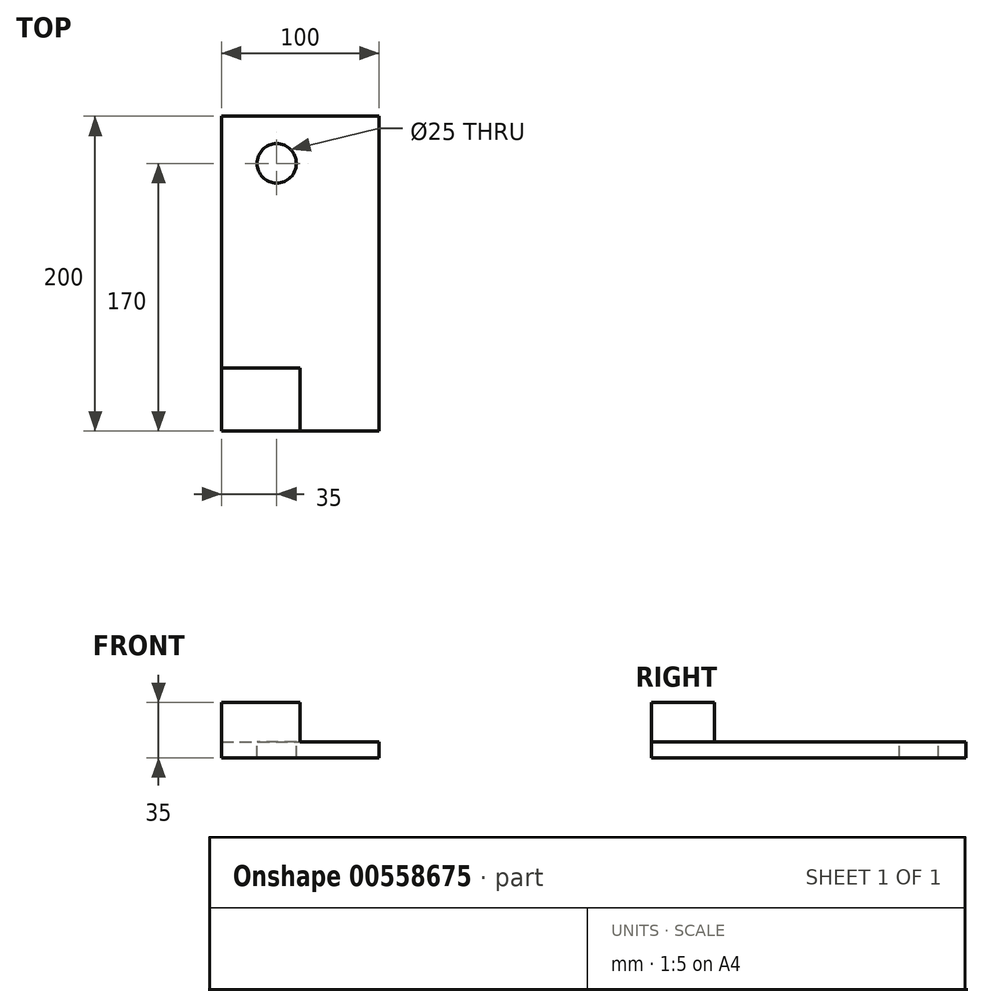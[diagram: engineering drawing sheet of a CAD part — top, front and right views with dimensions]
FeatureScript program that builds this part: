
annotation { "Feature Type Name" : "Feature", "Feature Type Description" : "" }
export const myFeature = defineFeature(function(context is Context, id is Id, definition is map)
    precondition{}
    {
        {
            var Q0;
            Q0=qCreatedBy(makeId("Top.planeOp"),FACE);
            var sketch = newSketch(context, id + "F0", { "sketchPlane" : qUnion([Q0])});
            skLineSegment(sketch, "E0.bottom", {"start": v(0, 0) * mm, "end": v(100, 0) * mm});
            skLineSegment(sketch, "E0.top", {"start": v(0, 200) * mm, "end": v(100, 200) * mm});
            skLineSegment(sketch, "E0.left", {"start": v(0, 0) * mm, "end": v(0, 200) * mm});
            skLineSegment(sketch, "E0.right", {"start": v(100, 0) * mm, "end": v(100, 200) * mm});
            skSolve(sketch);
        }
        {
            var Q0;
            Q0 = qSketchRegion(id + "F0", true);
            extrude(context, id + "F1", {"entities" : qUnion([Q0]), "depth" : 10 * mm, "offsetDistance" : 25 * mm});
        }
        {
            var Q0;
            Q0=makeQuery(id+"F1.opExtrude","CAP_FACE",FACE,{"disambiguationData":[OSD([sQuery(id+"F0.wireOp",EDGE,"E0.bottom"),sQuery(id+"F0.wireOp",EDGE,"E0.top"),sQuery(id+"F0.wireOp",EDGE,"E0.left"),sQuery(id+"F0.wireOp",EDGE,"E0.right")])],"isStart":false});
            var sketch = newSketch(context, id + "F2", { "sketchPlane" : qUnion([Q0])});
            skLineSegment(sketch, "E1.bottom", {"start": v(0, 0) * mm, "end": v(50, 0) * mm});
            skLineSegment(sketch, "E1.top", {"start": v(0, 40) * mm, "end": v(50, 40) * mm});
            skLineSegment(sketch, "E1.left", {"start": v(0, 0) * mm, "end": v(0, 40) * mm});
            skLineSegment(sketch, "E1.right", {"start": v(50, 0) * mm, "end": v(50, 40) * mm});
            skSolve(sketch);
        }
        {
            var Q0;
            Q0 = qSketchRegion(id + "F2", true);
            extrude(context, id + "F3", {"entities" : qUnion([Q0]), "operationType" : NewBodyOperationType.ADD, "depth" : 25 * mm, "offsetDistance" : 25 * mm});
        }
        {
            var Q0;
            Q0=makeQuery(id+"F1.opExtrude","CAP_FACE",FACE,{"disambiguationData":[OSD([sQuery(id+"F0.wireOp",EDGE,"E0.bottom"),sQuery(id+"F0.wireOp",EDGE,"E0.top"),sQuery(id+"F0.wireOp",EDGE,"E0.left"),sQuery(id+"F0.wireOp",EDGE,"E0.right")])],"isStart":false});
            var sketch = newSketch(context, id + "F4", { "sketchPlane" : qUnion([Q0])});
            skSolve(sketch);
        }
        {
            var Q0;
            Q0=makeQuery(id+"F4.imprint","IMPRINT",FACE,{"disambiguationData":[TD([[makeQuery(id+"F4.imprint","IMPRINT",EDGE,{"derivedFrom":makeQuery(id+"F1.opExtrude","CAP_EDGE",EDGE,{"disambiguationData":[OSD([sQuery(id+"F0.wireOp",EDGE,"E0.top")])],"isStart":false})}),-1.0]])]});
            var sketch = newSketch(context, id + "F5", { "sketchPlane" : qUnion([Q0])});
            skCircle(sketch, "E2", {"center": v(35, 170) * mm, "radius": 12.5 * mm});
            skSolve(sketch);
        }
        {
            var Q0;
            Q0 = qSketchRegion(id + "F5", true);
            extrude(context, id + "F6", {"entities" : qUnion([Q0]), "operationType" : NewBodyOperationType.REMOVE, "endBound" : BoundingType.THROUGH_ALL, "oppositeDirection" : true, "depth" : 25 * mm, "offsetDistance" : 25 * mm});
        }
    });
